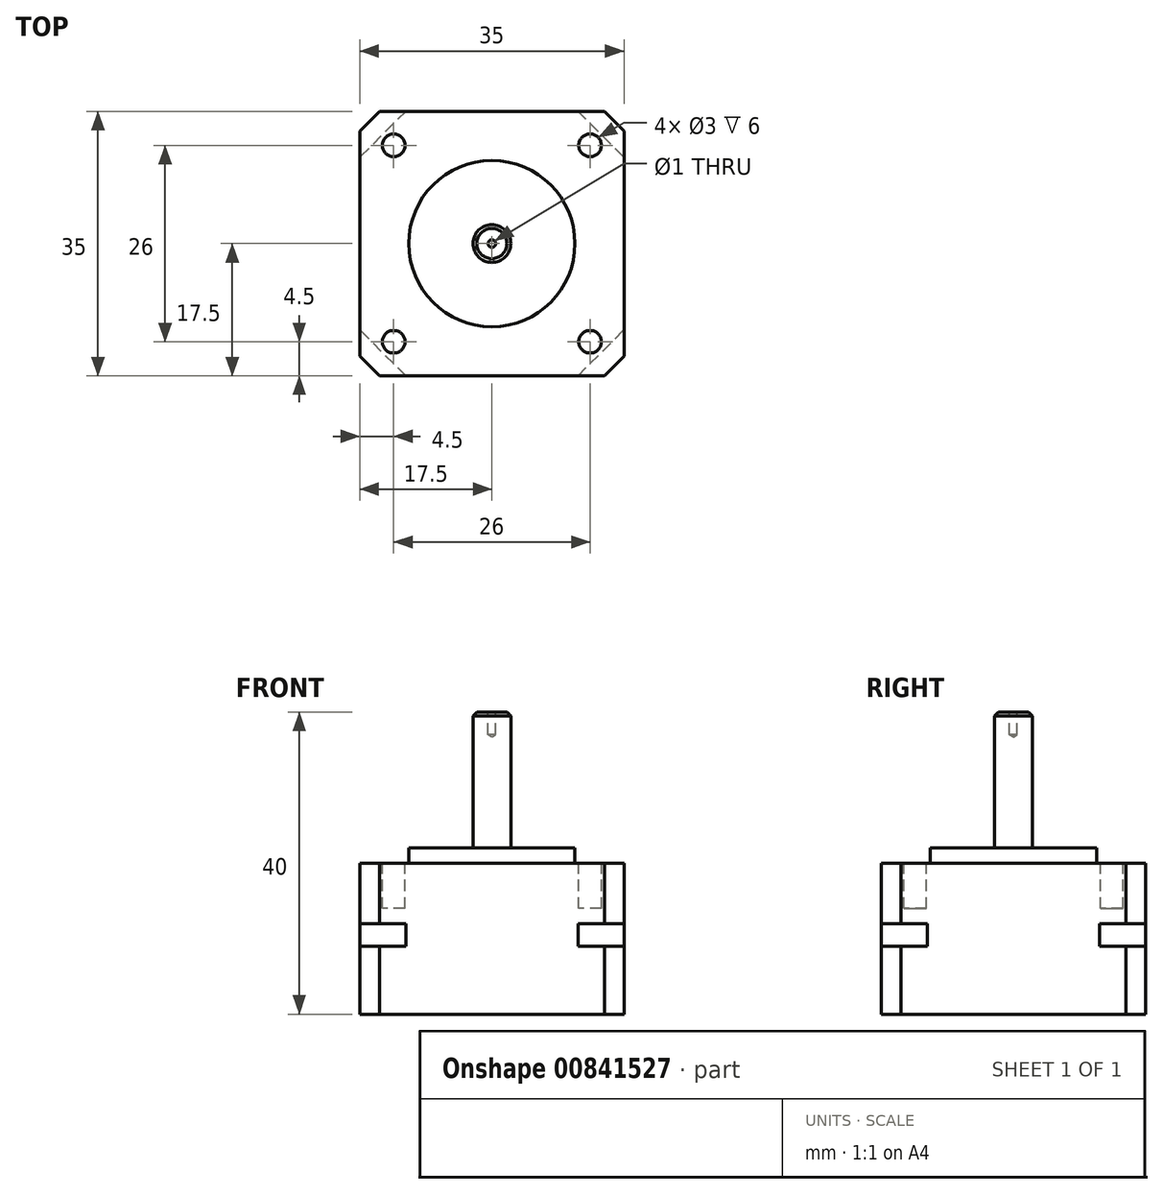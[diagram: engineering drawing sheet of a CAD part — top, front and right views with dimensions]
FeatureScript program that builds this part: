
annotation { "Feature Type Name" : "Feature", "Feature Type Description" : "" }
export const myFeature = defineFeature(function(context is Context, id is Id, definition is map)
    precondition{}
    {
        {
            var Q0;
            Q0=qCreatedBy(makeId("Top.planeOp"),FACE);
            var sketch = newSketch(context, id + "F0", { "sketchPlane" : qUnion([Q0])});
            skLineSegment(sketch, "E0.rect.bottom", {"start": v(-17.5, 17.5) * mm, "end": v(17.5, 17.5) * mm});
            skLineSegment(sketch, "E0.rect.top", {"start": v(-17.5, -17.5) * mm, "end": v(17.5, -17.5) * mm});
            skLineSegment(sketch, "E0.rect.left", {"start": v(-17.5, 17.5) * mm, "end": v(-17.5, -17.5) * mm});
            skLineSegment(sketch, "E0.rect.right", {"start": v(17.5, 17.5) * mm, "end": v(17.5, -17.5) * mm});
            skPoint(sketch, "E0.rect.middle", {"position": v(0, 0) * mm});
            skLineSegment(sketch, "E1", {"start": v(-17.5, 17.5) * mm, "end": v(17.5, -17.5) * mm, "construction": true});
            skSolve(sketch);
        }
        {
            var Q0;
            Q0=qSketchRegion(id+"F0",true);
            extrude(context, id + "F1", {"entities" : qUnion([Q0]), "endBound" : BoundingType.SYMMETRIC, "depth" : 3 * mm});
        }
        {
            var Q0;
            Q0=makeQuery(id+"F1.opExtrude","SWEPT_EDGE",EDGE,{"disambiguationData":[OSD([sQuery(id+"F0.wireOp",EDGE,"E0.rect.top"),sQuery(id+"F0.wireOp",EDGE,"E0.rect.left")])]});
            var Q1;
            Q1=makeQuery(id+"F1.opExtrude","SWEPT_EDGE",EDGE,{"disambiguationData":[OSD([sQuery(id+"F0.wireOp",EDGE,"E0.rect.top"),sQuery(id+"F0.wireOp",EDGE,"E0.rect.right")])]});
            var Q2;
            Q2=makeQuery(id+"F1.opExtrude","SWEPT_EDGE",EDGE,{"disambiguationData":[OSD([sQuery(id+"F0.wireOp",EDGE,"E0.rect.bottom"),sQuery(id+"F0.wireOp",EDGE,"E0.rect.right")])]});
            var Q3;
            Q3=makeQuery(id+"F1.opExtrude","SWEPT_EDGE",EDGE,{"disambiguationData":[OSD([sQuery(id+"F0.wireOp",EDGE,"E0.rect.bottom"),sQuery(id+"F0.wireOp",EDGE,"E0.rect.left")])]});
            chamfer(context, id + "F2", {"entities" : qUnion([Q0, Q1, Q2, Q3]), "width" : 6.1 * mm, "tangentPropagation" : true});
        }
        {
            var Q0;
            Q0=makeQuery(id+"F1.opExtrude","CAP_FACE",FACE,{"disambiguationData":[OSD([sQuery(id+"F0.wireOp",EDGE,"E0.rect.bottom"),sQuery(id+"F0.wireOp",EDGE,"E0.rect.top"),sQuery(id+"F0.wireOp",EDGE,"E0.rect.left"),sQuery(id+"F0.wireOp",EDGE,"E0.rect.right")])],"isStart":false});
            var sketch = newSketch(context, id + "F3", { "sketchPlane" : qUnion([Q0])});
            skLineSegment(sketch, "E2.0", {"start": v(-17.5, 17.5) * mm, "end": v(17.5, 17.5) * mm});
            skLineSegment(sketch, "E2.1", {"start": v(-17.5, -17.5) * mm, "end": v(17.5, -17.5) * mm});
            skLineSegment(sketch, "E2.2", {"start": v(-17.5, 17.5) * mm, "end": v(-17.5, -17.5) * mm});
            skLineSegment(sketch, "E2.3", {"start": v(17.5, 17.5) * mm, "end": v(17.5, -17.5) * mm});
            skPoint(sketch, "E2.4", {"position": v(0, 0) * mm});
            skSolve(sketch);
        }
        {
            var Q0;
            Q0=qSketchRegion(id+"F3",true);
            extrude(context, id + "F4", {"entities" : qUnion([Q0]), "operationType" : NewBodyOperationType.ADD, "depth" : 8 * mm});
        }
        {
            var Q0;
            Q0=makeQuery(id+"F4.opExtrude","SWEPT_EDGE",EDGE,{"disambiguationData":[OSD([sQuery(id+"F3.wireOp",EDGE,"E2.1"),sQuery(id+"F3.wireOp",EDGE,"E2.2")])]});
            var Q1;
            Q1=makeQuery(id+"F4.opExtrude","SWEPT_EDGE",EDGE,{"disambiguationData":[OSD([sQuery(id+"F3.wireOp",EDGE,"E2.1"),sQuery(id+"F3.wireOp",EDGE,"E2.3")])]});
            var Q2;
            Q2=makeQuery(id+"F4.opExtrude","SWEPT_EDGE",EDGE,{"disambiguationData":[OSD([sQuery(id+"F3.wireOp",EDGE,"E2.0"),sQuery(id+"F3.wireOp",EDGE,"E2.3")])]});
            var Q3;
            Q3=makeQuery(id+"F4.opExtrude","SWEPT_EDGE",EDGE,{"disambiguationData":[OSD([sQuery(id+"F3.wireOp",EDGE,"E2.0"),sQuery(id+"F3.wireOp",EDGE,"E2.2")])]});
            chamfer(context, id + "F5", {"entities" : qUnion([Q0, Q1, Q2, Q3]), "width" : 2.6 * mm, "tangentPropagation" : true});
        }
        {
            var Q0;
            Q0=makeQuery(id+"F1.opExtrude","CAP_FACE",FACE,{"disambiguationData":[OSD([sQuery(id+"F0.wireOp",EDGE,"E0.rect.bottom"),sQuery(id+"F0.wireOp",EDGE,"E0.rect.top"),sQuery(id+"F0.wireOp",EDGE,"E0.rect.left"),sQuery(id+"F0.wireOp",EDGE,"E0.rect.right")])],"isStart":true});
            var sketch = newSketch(context, id + "F6", { "sketchPlane" : qUnion([Q0])});
            skLineSegment(sketch, "E3.0.0", {"start": v(14.9, -17.5) * mm, "end": v(-14.9, -17.5) * mm});
            skLineSegment(sketch, "E3.0.1", {"start": v(-14.9, -17.5) * mm, "end": v(-17.5, -14.9) * mm});
            skLineSegment(sketch, "E3.0.2", {"start": v(-17.5, -14.9) * mm, "end": v(-17.5, 14.9) * mm});
            skLineSegment(sketch, "E3.0.3", {"start": v(-17.5, 14.9) * mm, "end": v(-14.9, 17.5) * mm});
            skLineSegment(sketch, "E3.0.4", {"start": v(-14.9, 17.5) * mm, "end": v(14.9, 17.5) * mm});
            skLineSegment(sketch, "E3.0.5", {"start": v(14.9, 17.5) * mm, "end": v(17.5, 14.9) * mm});
            skLineSegment(sketch, "E3.0.6", {"start": v(17.5, 14.9) * mm, "end": v(17.5, -14.9) * mm});
            skLineSegment(sketch, "E3.0.7", {"start": v(17.5, -14.9) * mm, "end": v(14.9, -17.5) * mm});
            skSolve(sketch);
        }
        {
            var Q0;
            Q0=qSketchRegion(id+"F6",true);
            extrude(context, id + "F7", {"entities" : qUnion([Q0]), "operationType" : NewBodyOperationType.ADD, "depth" : 9 * mm});
        }
        {
            var Q0;
            Q0=makeQuery(id+"F4.opExtrude","CAP_FACE",FACE,{"disambiguationData":[OSD([sQuery(id+"F3.wireOp",EDGE,"E2.0"),sQuery(id+"F3.wireOp",EDGE,"E2.1"),sQuery(id+"F3.wireOp",EDGE,"E2.2"),sQuery(id+"F3.wireOp",EDGE,"E2.3")])],"isStart":false});
            var sketch = newSketch(context, id + "F8", { "sketchPlane" : qUnion([Q0])});
            skCircle(sketch, "E4", {"center": v(0, 0) * mm, "radius": 11 * mm});
            skSolve(sketch);
        }
        {
            var Q0;
            Q0=qSketchRegion(id+"F8",true);
            extrude(context, id + "F9", {"entities" : qUnion([Q0]), "operationType" : NewBodyOperationType.ADD, "depth" : 2 * mm, "offsetDistance" : 25 * mm});
        }
        {
            var Q0;
            Q0=makeQuery(id+"F9.opExtrude","CAP_FACE",FACE,{"disambiguationData":[OSD([sQuery(id+"F8.wireOp",EDGE,"E4")])],"isStart":false});
            var sketch = newSketch(context, id + "F10", { "sketchPlane" : qUnion([Q0])});
            skCircle(sketch, "E5", {"center": v(0, 0) * mm, "radius": 2.5 * mm});
            skSolve(sketch);
        }
        {
            var Q0;
            Q0=makeQuery(id+"F10.imprint","IMPRINT",FACE,{"disambiguationData":[TD([[makeQuery(id+"F10.imprint","IMPRINT",EDGE,{"derivedFrom":sQuery(id+"F10.wireOp",EDGE,"E5")}),1.0]])]});
            extrude(context, id + "F11", {"entities" : qUnion([Q0]), "operationType" : NewBodyOperationType.ADD, "depth" : 18 * mm});
        }
        {
            var Q0;
            Q0=makeQuery(id+"F4.opExtrude","CAP_FACE",FACE,{"disambiguationData":[OSD([sQuery(id+"F3.wireOp",EDGE,"E2.0"),sQuery(id+"F3.wireOp",EDGE,"E2.1"),sQuery(id+"F3.wireOp",EDGE,"E2.2"),sQuery(id+"F3.wireOp",EDGE,"E2.3")])],"isStart":false});
            var sketch = newSketch(context, id + "F12", { "sketchPlane" : qUnion([Q0])});
            skCircle(sketch, "E6", {"center": v(-13, 13) * mm, "radius": 1.5 * mm});
            skCircle(sketch, "E7.MirrorC", {"center": v(13, 13) * mm, "radius": 1.5 * mm});
            skCircle(sketch, "E8.MirrorC", {"center": v(-13, -13) * mm, "radius": 1.5 * mm});
            skCircle(sketch, "E9.MirrorC", {"center": v(13, -13) * mm, "radius": 1.5 * mm});
            skLineSegment(sketch, "E10", {"start": v(-13, 13) * mm, "end": v(13, -13) * mm, "construction": true});
            skLineSegment(sketch, "E11.rect.bottom", {"start": v(-13, 13) * mm, "end": v(13, 13) * mm, "construction": true});
            skLineSegment(sketch, "E11.rect.top", {"start": v(-13, -13) * mm, "end": v(13, -13) * mm, "construction": true});
            skLineSegment(sketch, "E11.rect.left", {"start": v(-13, 13) * mm, "end": v(-13, -13) * mm, "construction": true});
            skLineSegment(sketch, "E11.rect.right", {"start": v(13, 13) * mm, "end": v(13, -13) * mm, "construction": true});
            skPoint(sketch, "E11.rect.middle", {"position": v(0, 0) * mm});
            skSolve(sketch);
        }
        {
            var Q0;
            Q0=qSketchRegion(id+"F12",true);
            extrude(context, id + "F13", {"entities" : qUnion([Q0]), "operationType" : NewBodyOperationType.REMOVE, "oppositeDirection" : true, "depth" : 6 * mm});
        }
        {
            var Q0;
            Q0=makeQuery(id+"F11.opExtrude","CAP_FACE",FACE,{"disambiguationData":[OSD([sQuery(id+"F10.wireOp",EDGE,"E5")])],"isStart":false});
            chamfer(context, id + "F14", {"entities" : qUnion([Q0]), "width" : 0.5 * mm, "tangentPropagation" : true});
        }
        {
            var Q0;
            Q0=makeQuery(id+"F11.opExtrude","CAP_FACE",FACE,{"disambiguationData":[OSD([sQuery(id+"F10.wireOp",EDGE,"E5")])],"isStart":false});
            var sketch = newSketch(context, id + "F15", { "sketchPlane" : qUnion([Q0])});
            skPoint(sketch, "E12", {"position": v(0, 0) * mm});
            skSolve(sketch);
        }
        {
            var Q0;
            Q0=sQuery(id+"F15.wireOp",VERTEX,"E12");
            var Q1;
            Q1=makeQuery(id+"F1.opExtrude","SWEPT_BODY",BODY,{"disambiguationData":[OSD([sQuery(id+"F0.wireOp",EDGE,"E0.rect.bottom"),sQuery(id+"F0.wireOp",EDGE,"E0.rect.top"),sQuery(id+"F0.wireOp",EDGE,"E0.rect.left"),sQuery(id+"F0.wireOp",EDGE,"E0.rect.right")])]});
            hole(context, id + "F16", {"style" : HoleStyle.SIMPLE, "holeDiameter" : 1 * mm, "endStyle" : HoleEndStyle.BLIND, "holeDepth" : 3 * mm, "locations" : qUnion([Q0]), "scope" : qUnion([Q1])});
        }
    });
